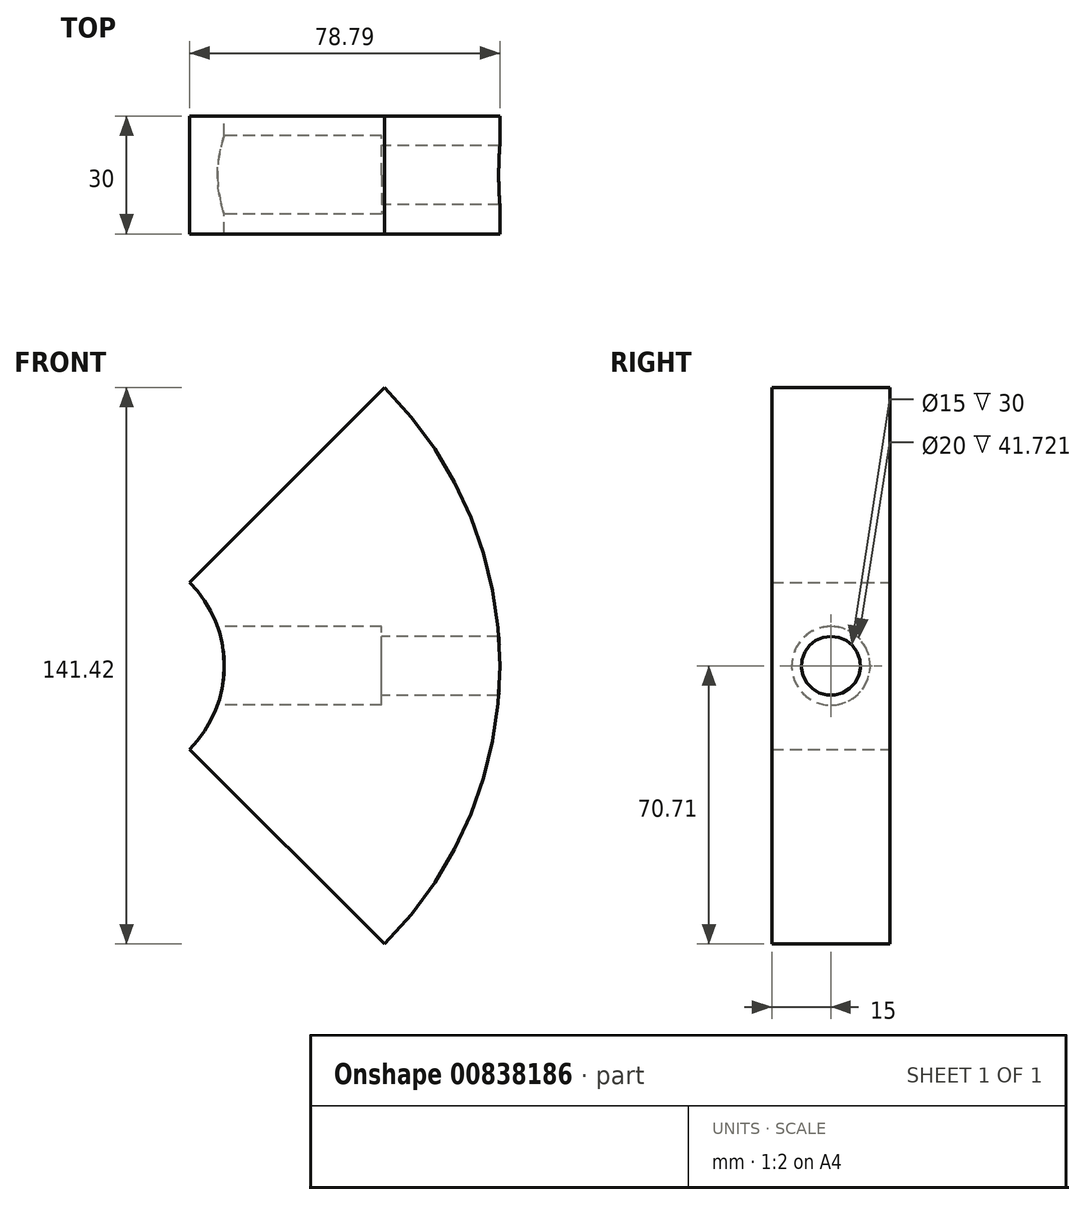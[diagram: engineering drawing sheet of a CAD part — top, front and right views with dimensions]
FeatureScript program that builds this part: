
annotation { "Feature Type Name" : "Feature", "Feature Type Description" : "" }
export const myFeature = defineFeature(function(context is Context, id is Id, definition is map)
    precondition{}
    {
        {
            var Q0;
            Q0=qCreatedBy(makeId("Front.planeOp"),FACE);
            var sketch = newSketch(context, id + "F0", { "sketchPlane" : qUnion([Q0])});
            skArc(sketch, "E0", {"start": v(21.21, -21.21) * mm, "mid": v(30, 0) * mm, "end": v(21.21, 21.21) * mm});
            skLineSegment(sketch, "E1.5.0", {"start": v(70.71, -70.71) * mm, "end": v(21.21, -21.21) * mm});
            skLineSegment(sketch, "E1.7.0", {"start": v(70.71, 70.71) * mm, "end": v(21.21, 21.21) * mm});
            skPoint(sketch, "E2.orphan", {"position": v(0, 100) * mm});
            skLineSegment(sketch, "E3.trimOffspring", {"start": v(21.21, -21.21) * mm, "end": v(70.71, -70.71) * mm});
            skLineSegment(sketch, "E4.trimOffspring", {"start": v(21.21, 21.21) * mm, "end": v(70.71, 70.71) * mm});
            skPoint(sketch, "E5.orphan", {"position": v(-100, 0) * mm});
            skArc(sketch, "E6.trimOffspring", {"start": v(70.71, -70.71) * mm, "mid": v(100, 0) * mm, "end": v(70.71, 70.71) * mm});
            skSolve(sketch);
        }
        {
            var Q0;
            Q0 = qSketchRegion(id + "F0", true);
            extrude(context, id + "F1", {"entities" : qUnion([Q0]), "endBound" : BoundingType.SYMMETRIC, "depth" : 30 * mm, "offsetDistance" : 25 * mm});
        }
        {
            var Q0;
            Q0=qCreatedBy(makeId("Right.planeOp"),FACE);
            var sketch = newSketch(context, id + "F2", { "sketchPlane" : qUnion([Q0])});
            skCircle(sketch, "E7", {"center": v(0, 0) * mm, "radius": 7.5 * mm});
            skSolve(sketch);
        }
        {
            var Q0;
            Q0 = qSketchRegion(id + "F2", true);
            extrude(context, id + "F3", {"entities" : qUnion([Q0]), "operationType" : NewBodyOperationType.REMOVE, "depth" : 118.47 * mm, "offsetDistance" : 25 * mm});
        }
        {
            var Q0;
            Q0=qCreatedBy(makeId("Right.planeOp"),FACE);
            var sketch = newSketch(context, id + "F4", { "sketchPlane" : qUnion([Q0])});
            skCircle(sketch, "E8", {"center": v(0, 0) * mm, "radius": 10 * mm});
            skSolve(sketch);
        }
        {
            var Q0;
            Q0=makeQuery(id+"F4.imprint","IMPRINT",FACE,{"disambiguationData":[TD([[makeQuery(id+"F4.imprint","IMPRINT",EDGE,{"derivedFrom":sQuery(id+"F4.wireOp",EDGE,"E8")}),1.0]])]});
            extrude(context, id + "F5", {"entities" : qUnion([Q0]), "operationType" : NewBodyOperationType.REMOVE, "depth" : 70 * mm, "offsetDistance" : 25 * mm});
        }
    });
